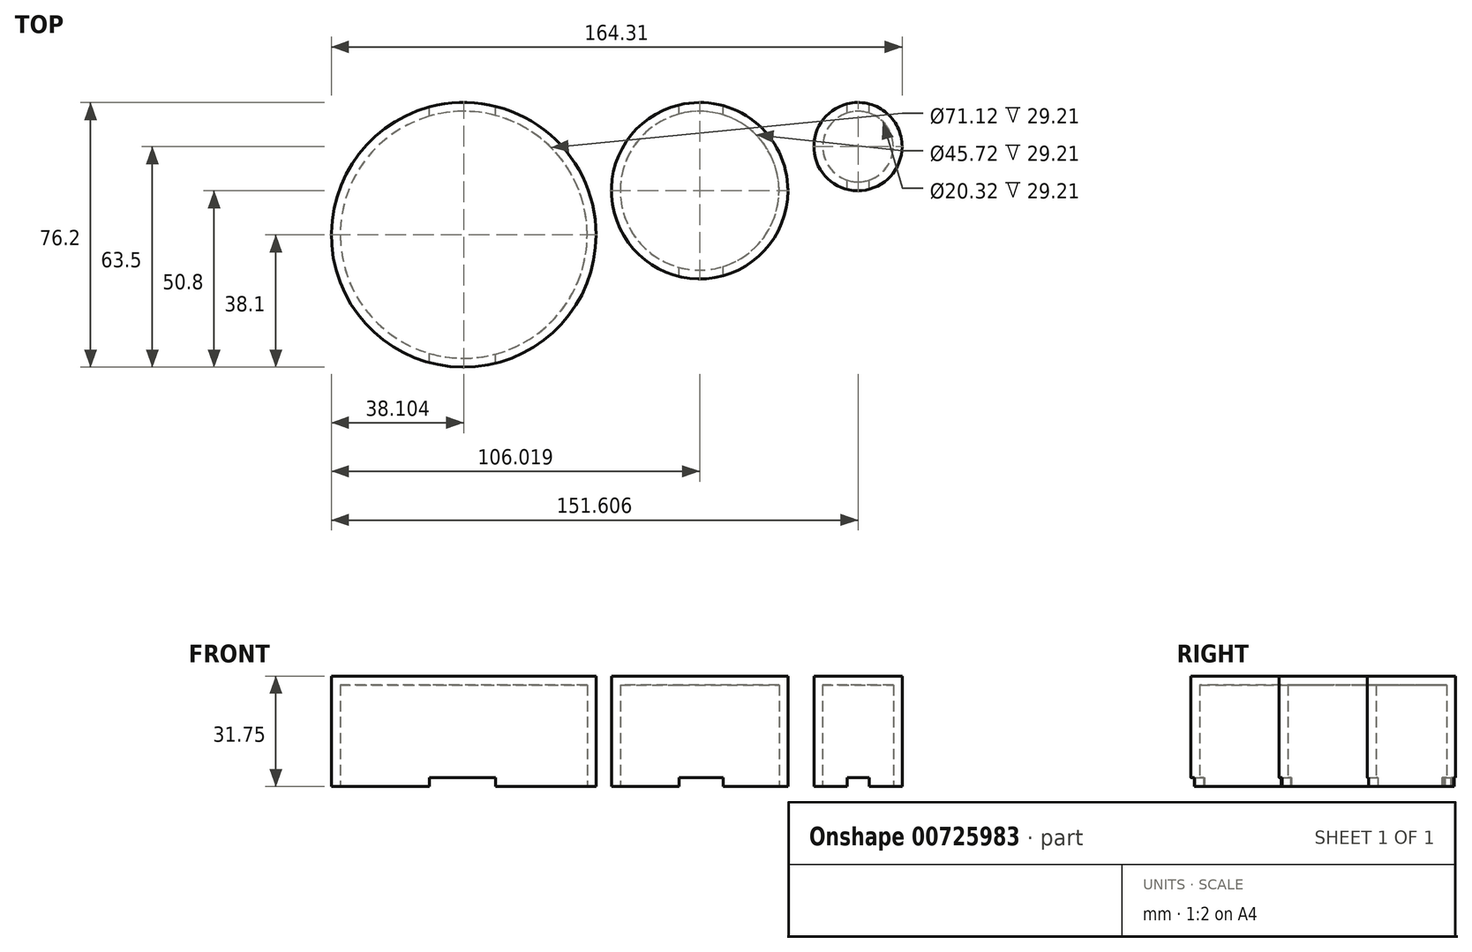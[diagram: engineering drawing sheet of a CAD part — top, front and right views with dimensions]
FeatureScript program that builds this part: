
annotation { "Feature Type Name" : "Feature", "Feature Type Description" : "" }
export const myFeature = defineFeature(function(context is Context, id is Id, definition is map)
    precondition{}
    {
        {
            var Q0;
            Q0=qCreatedBy(makeId("Top.planeOp"),FACE);
            var sketch = newSketch(context, id + "F0", { "sketchPlane" : qUnion([Q0])});
            skCircle(sketch, "E0", {"center": v(-54.08, -38.1) * mm, "radius": 38.1 * mm});
            skCircle(sketch, "E1", {"center": v(13.84, -25.4) * mm, "radius": 25.4 * mm});
            skCircle(sketch, "E2", {"center": v(59.43, -12.7) * mm, "radius": 12.7 * mm});
            skLineSegment(sketch, "E3", {"start": v(-102.92, 0) * mm, "end": v(105.01, 0) * mm, "construction": true});
            skSolve(sketch);
        }
        {
            var Q0;
            Q0 = qSketchRegion(id + "F0", true);
            extrude(context, id + "F1", {"entities" : qUnion([Q0]), "depth" : 31.75 * mm, "offsetDistance" : 25.4 * mm});
        }
        {
            var Q0;
            Q0=makeQuery(id+"F1.opExtrude","CAP_FACE",FACE,{"disambiguationData":[OSD([sQuery(id+"F0.wireOp",EDGE,"E1")])],"isStart":true});
            var Q1;
            Q1=makeQuery(id+"F1.opExtrude","CAP_FACE",FACE,{"disambiguationData":[OSD([sQuery(id+"F0.wireOp",EDGE,"E2")])],"isStart":true});
            var Q2;
            Q2=makeQuery(id+"F1.opExtrude","CAP_FACE",FACE,{"disambiguationData":[OSD([sQuery(id+"F0.wireOp",EDGE,"E0")])],"isStart":true});
            shell(context, id + "F2", {"entities" : qUnion([Q0, Q1, Q2]), "thickness" : 2.54 * mm});
        }
        {
            var Q0;
            Q0=qCreatedBy(makeId("Front.planeOp"),FACE);
            var sketch = newSketch(context, id + "F3", { "sketchPlane" : qUnion([Q0])});
            skLineSegment(sketch, "E4.bottom", {"start": v(62.68, 0) * mm, "end": v(56.33, 0) * mm});
            skLineSegment(sketch, "E4.top", {"start": v(62.68, 2.54) * mm, "end": v(56.33, 2.54) * mm});
            skLineSegment(sketch, "E4.left", {"start": v(62.68, 0) * mm, "end": v(62.68, 2.54) * mm});
            skLineSegment(sketch, "E4.right", {"start": v(56.33, 0) * mm, "end": v(56.33, 2.54) * mm});
            skLineSegment(sketch, "E5.bottom", {"start": v(20.63, 0) * mm, "end": v(7.93, 0) * mm});
            skLineSegment(sketch, "E5.top", {"start": v(20.63, 2.54) * mm, "end": v(7.93, 2.54) * mm});
            skLineSegment(sketch, "E5.left", {"start": v(20.63, 0) * mm, "end": v(20.63, 2.54) * mm});
            skLineSegment(sketch, "E5.right", {"start": v(7.93, 0) * mm, "end": v(7.93, 2.54) * mm});
            skLineSegment(sketch, "E6.bottom", {"start": v(-44.95, 0) * mm, "end": v(-64, 0) * mm});
            skLineSegment(sketch, "E6.top", {"start": v(-44.95, 2.54) * mm, "end": v(-64, 2.54) * mm});
            skLineSegment(sketch, "E6.left", {"start": v(-44.95, 0) * mm, "end": v(-44.95, 2.54) * mm});
            skLineSegment(sketch, "E6.right", {"start": v(-64, 0) * mm, "end": v(-64, 2.54) * mm});
            skSolve(sketch);
        }
        {
            var Q0;
            Q0 = qSketchRegion(id + "F3", true);
            extrude(context, id + "F4", {"entities" : qUnion([Q0]), "operationType" : NewBodyOperationType.REMOVE, "depth" : 88.9 * mm, "offsetDistance" : 25.4 * mm});
        }
    });
